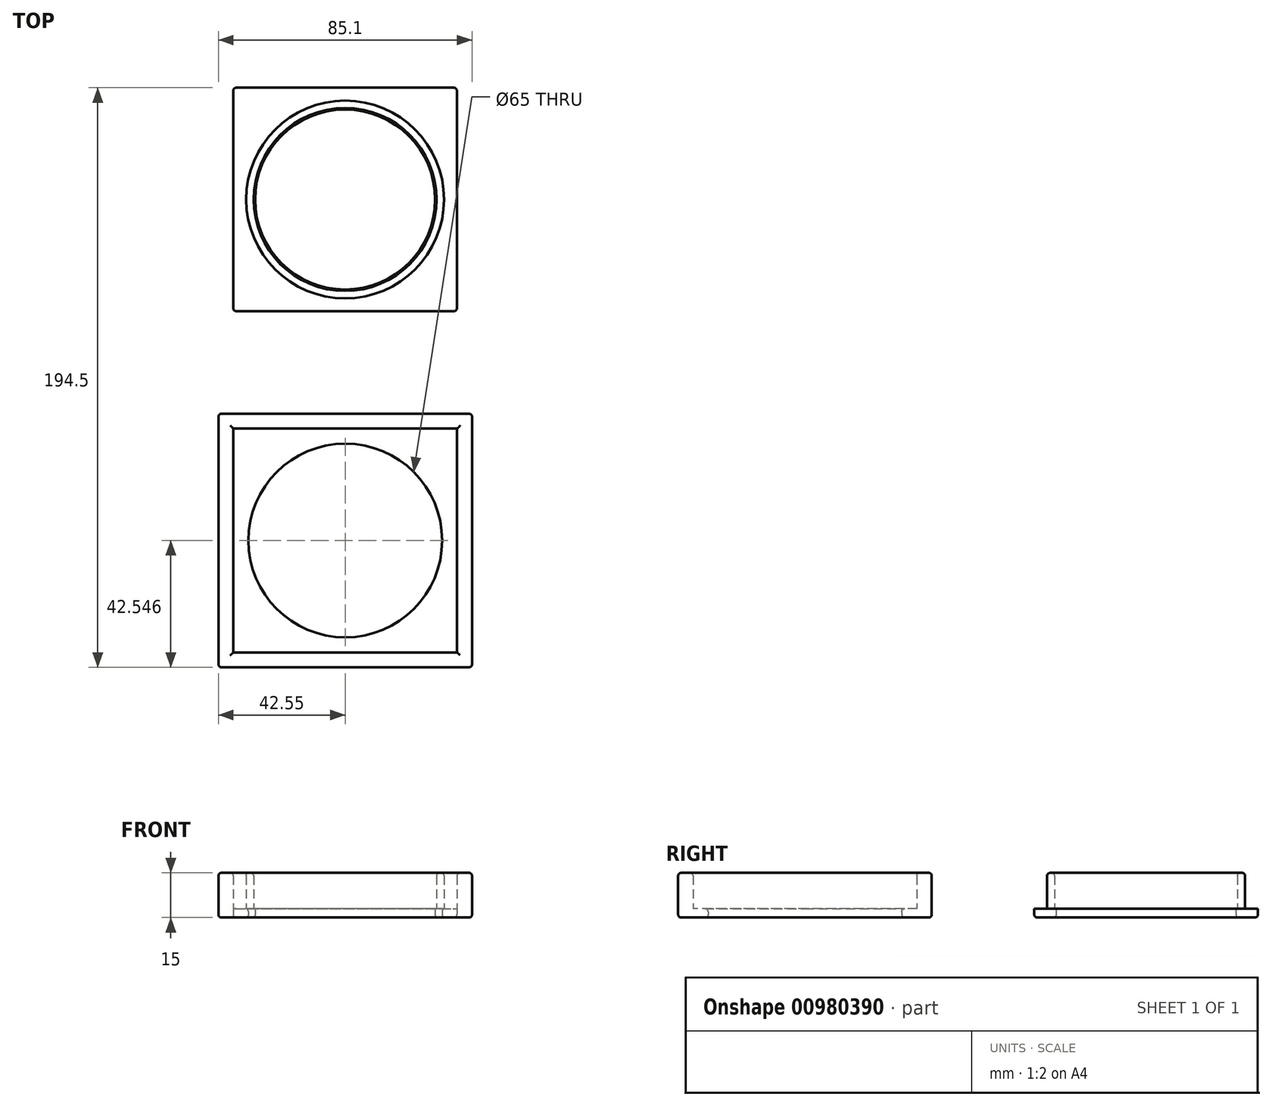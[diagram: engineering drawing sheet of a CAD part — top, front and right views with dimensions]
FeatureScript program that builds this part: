
annotation { "Feature Type Name" : "Feature", "Feature Type Description" : "" }
export const myFeature = defineFeature(function(context is Context, id is Id, definition is map)
    precondition{}
    {
        {
            var Q0;
            Q0=qCreatedBy(makeId("Top.planeOp"),FACE);
            var sketch = newSketch(context, id + "F0", { "sketchPlane" : qUnion([Q0])});
            skLineSegment(sketch, "E0.bottom", {"start": v(0, 0) * mm, "end": v(75, 0) * mm});
            skLineSegment(sketch, "E0.top", {"start": v(0, 75) * mm, "end": v(75, 75) * mm});
            skLineSegment(sketch, "E0.left", {"start": v(0, 0) * mm, "end": v(0, 75) * mm});
            skLineSegment(sketch, "E0.right", {"start": v(75, 0) * mm, "end": v(75, 75) * mm});
            skCircle(sketch, "E1", {"center": v(37.5, 37.5) * mm, "radius": 30.7 * mm});
            skPoint(sketch, "E1.centerSnap0", {"position": v(37.5, 75) * mm});
            skPoint(sketch, "E1.centerSnap1", {"position": v(0, 37.5) * mm});
            skCircle(sketch, "E2", {"center": v(37.5, 37.5) * mm, "radius": 30.2 * mm});
            skCircle(sketch, "E3", {"center": v(37.5, 37.5) * mm, "radius": 33.2 * mm});
            skCircle(sketch, "E4", {"center": v(37.55, -76.95) * mm, "radius": 32.5 * mm});
            skPoint(sketch, "E4.centerSnap1", {"position": v(37.55, -39.4) * mm});
            skLineSegment(sketch, "E5.0", {"start": v(-5, -34.4) * mm, "end": v(80.1, -34.4) * mm});
            skLineSegment(sketch, "E5.1", {"start": v(-5, -34.4) * mm, "end": v(-5, -119.5) * mm});
            skLineSegment(sketch, "E5.2", {"start": v(-5, -119.5) * mm, "end": v(80.1, -119.5) * mm});
            skLineSegment(sketch, "E5.3", {"start": v(80.1, -34.4) * mm, "end": v(80.1, -119.5) * mm});
            skLineSegment(sketch, "E6", {"start": v(0, -114.5) * mm, "end": v(75.1, -114.5) * mm});
            skLineSegment(sketch, "E7", {"start": v(75.1, -39.4) * mm, "end": v(75.1, -114.5) * mm});
            skLineSegment(sketch, "E8", {"start": v(0, -39.4) * mm, "end": v(0, -114.5) * mm});
            skLineSegment(sketch, "E9", {"start": v(0, -39.4) * mm, "end": v(75.1, -39.4) * mm});
            skPoint(sketch, "E10", {"position": v(-5, -76.95) * mm});
            skPoint(sketch, "E11", {"position": v(37.55, -34.4) * mm});
            skSolve(sketch);
        }
        {
            var Q0;
            Q0=makeQuery(id+"F0.imprint","IMPRINT",FACE,{"disambiguationData":[TD([[makeQuery(id+"F0.imprint","IMPRINT",EDGE,{"derivedFrom":sQuery(id+"F0.wireOp",EDGE,"E1")}),-1.0]])]});
            var Q1;
            Q1=makeQuery(id+"F0.imprint","IMPRINT",FACE,{"disambiguationData":[TD([[makeQuery(id+"F0.imprint","IMPRINT",EDGE,{"derivedFrom":sQuery(id+"F0.wireOp",EDGE,"JDFHyrcC-VGeh-v9XD-pVOG-qxKent8c7stP.bottom")}),1.0]])]});
            var Q2;
            Q2=makeQuery(id+"F0.imprint","IMPRINT",FACE,{"disambiguationData":[TD([[makeQuery(id+"F0.imprint","IMPRINT",EDGE,{"derivedFrom":sQuery(id+"F0.wireOp",EDGE,"E5.0")}),-1.0]])]});
            extrude(context, id + "F1", {"entities" : qUnion([Q0, Q1, Q2]), "depth" : 15 * mm, "offsetDistance" : 25 * mm});
        }
        {
            var Q0;
            Q0=makeQuery(id+"F0.imprint","IMPRINT",FACE,{"disambiguationData":[TD([[makeQuery(id+"F0.imprint","IMPRINT",EDGE,{"derivedFrom":sQuery(id+"F0.wireOp",EDGE,"E1")}),1.0]])]});
            var Q1;
            Q1=makeQuery(id+"F0.imprint","IMPRINT",FACE,{"disambiguationData":[TD([[makeQuery(id+"F0.imprint","IMPRINT",EDGE,{"derivedFrom":sQuery(id+"F0.wireOp",EDGE,"E0.bottom")}),1.0]])]});
            var Q2;
            Q2=makeQuery(id+"F0.imprint","IMPRINT",FACE,{"disambiguationData":[TD([[makeQuery(id+"F0.imprint","IMPRINT",EDGE,{"derivedFrom":sQuery(id+"F0.wireOp",EDGE,"JDFHyrcC-VGeh-v9XD-pVOG-qxKent8c7stP.bottom")}),-1.0]])]});
            var Q3;
            Q3=makeQuery(id+"F0.imprint","IMPRINT",FACE,{"disambiguationData":[TD([[makeQuery(id+"F0.imprint","IMPRINT",EDGE,{"derivedFrom":sQuery(id+"F0.wireOp",EDGE,"E4")}),-1.0]])]});
            extrude(context, id + "F2", {"entities" : qUnion([Q0, Q1, Q2, Q3]), "operationType" : NewBodyOperationType.ADD, "depth" : 3 * mm, "offsetDistance" : 25 * mm});
        }
        {
            var Q0;
            Q0=makeQuery(id+"F1.opExtrude","CAP_EDGE",EDGE,{"disambiguationData":[OSD([sQuery(id+"F0.wireOp",EDGE,"E1")])],"isStart":false});
            var Q1;
            Q1=makeQuery(id+"F1.opExtrude","CAP_EDGE",EDGE,{"disambiguationData":[OSD([sQuery(id+"F0.wireOp",EDGE,"E3")])],"isStart":false});
            var Q2;
            Q2=makeQuery(id+"F2.opExtrude","CAP_EDGE",EDGE,{"disambiguationData":[OSD([sQuery(id+"F0.wireOp",EDGE,"E0.bottom")])],"isStart":true});
            var Q3;
            Q3=makeQuery(id+"F2.opExtrude","CAP_EDGE",EDGE,{"disambiguationData":[OSD([sQuery(id+"F0.wireOp",EDGE,"E0.right")])],"isStart":true});
            var Q4;
            Q4=makeQuery(id+"F2.opExtrude","CAP_EDGE",EDGE,{"disambiguationData":[OSD([sQuery(id+"F0.wireOp",EDGE,"E0.top")])],"isStart":true});
            var Q5;
            Q5=makeQuery(id+"F2.opExtrude","CAP_EDGE",EDGE,{"disambiguationData":[OSD([sQuery(id+"F0.wireOp",EDGE,"E0.left")])],"isStart":true});
            var Q6;
            Q6=makeQuery(id+"F2.opExtrude","CAP_EDGE",EDGE,{"disambiguationData":[OSD([sQuery(id+"F0.wireOp",EDGE,"E2")])],"isStart":true});
            var Q7;
            Q7=makeQuery(id+"F1.opExtrude","CAP_EDGE",EDGE,{"disambiguationData":[OSD([sQuery(id+"F0.wireOp",EDGE,"E5.3")])],"isStart":false});
            var Q8;
            Q8=makeQuery(id+"F1.opExtrude","CAP_EDGE",EDGE,{"disambiguationData":[OSD([sQuery(id+"F0.wireOp",EDGE,"E5.0")])],"isStart":false});
            var Q9;
            Q9=makeQuery(id+"F1.opExtrude","CAP_EDGE",EDGE,{"disambiguationData":[OSD([sQuery(id+"F0.wireOp",EDGE,"E5.1")])],"isStart":false});
            var Q10;
            Q10=makeQuery(id+"F1.opExtrude","CAP_EDGE",EDGE,{"disambiguationData":[OSD([sQuery(id+"F0.wireOp",EDGE,"E5.2")])],"isStart":false});
            var Q11;
            Q11=makeQuery(id+"F1.opExtrude","SWEPT_EDGE",EDGE,{"disambiguationData":[OSD([sQuery(id+"F0.wireOp",EDGE,"E5.1"),sQuery(id+"F0.wireOp",EDGE,"E5.2")])]});
            var Q12;
            Q12=makeQuery(id+"F1.opExtrude","SWEPT_EDGE",EDGE,{"disambiguationData":[OSD([sQuery(id+"F0.wireOp",EDGE,"E5.2"),sQuery(id+"F0.wireOp",EDGE,"E5.3")])]});
            var Q13;
            Q13=makeQuery(id+"F1.opExtrude","SWEPT_EDGE",EDGE,{"disambiguationData":[OSD([sQuery(id+"F0.wireOp",EDGE,"E5.0"),sQuery(id+"F0.wireOp",EDGE,"E5.3")])]});
            var Q14;
            Q14=makeQuery(id+"F1.opExtrude","SWEPT_EDGE",EDGE,{"disambiguationData":[OSD([sQuery(id+"F0.wireOp",EDGE,"E5.0"),sQuery(id+"F0.wireOp",EDGE,"E5.1")])]});
            var Q15;
            Q15=makeQuery(id+"F1.opExtrude","CAP_EDGE",EDGE,{"disambiguationData":[OSD([sQuery(id+"F0.wireOp",EDGE,"E5.0")])],"isStart":true});
            var Q16;
            Q16=makeQuery(id+"F1.opExtrude","CAP_EDGE",EDGE,{"disambiguationData":[OSD([sQuery(id+"F0.wireOp",EDGE,"E5.3")])],"isStart":true});
            var Q17;
            Q17=makeQuery(id+"F2.opExtrude","CAP_EDGE",EDGE,{"disambiguationData":[OSD([sQuery(id+"F0.wireOp",EDGE,"E4")])],"isStart":true});
            var Q18;
            Q18=makeQuery(id+"F1.opExtrude","CAP_EDGE",EDGE,{"disambiguationData":[OSD([sQuery(id+"F0.wireOp",EDGE,"E5.1")])],"isStart":true});
            var Q19;
            Q19=makeQuery(id+"F1.opExtrude","CAP_EDGE",EDGE,{"disambiguationData":[OSD([sQuery(id+"F0.wireOp",EDGE,"E5.2")])],"isStart":true});
            var Q20;
            Q20=makeQuery(id+"F2.opExtrude","CAP_EDGE",EDGE,{"disambiguationData":[OSD([sQuery(id+"F0.wireOp",EDGE,"E4")])],"isStart":false});
            var Q21;
            Q21=makeQuery(id+"F2.opExtrude","SWEPT_EDGE",EDGE,{"disambiguationData":[OSD([sQuery(id+"F0.wireOp",EDGE,"E0.top"),sQuery(id+"F0.wireOp",EDGE,"E0.right")])]});
            var Q22;
            Q22=makeQuery(id+"F2.opExtrude","SWEPT_EDGE",EDGE,{"disambiguationData":[OSD([sQuery(id+"F0.wireOp",EDGE,"E0.top"),sQuery(id+"F0.wireOp",EDGE,"E0.left")])]});
            var Q23;
            Q23=makeQuery(id+"F2.opExtrude","SWEPT_EDGE",EDGE,{"disambiguationData":[OSD([sQuery(id+"F0.wireOp",EDGE,"E0.bottom"),sQuery(id+"F0.wireOp",EDGE,"E0.left")])]});
            var Q24;
            Q24=makeQuery(id+"F2.opExtrude","SWEPT_EDGE",EDGE,{"disambiguationData":[OSD([sQuery(id+"F0.wireOp",EDGE,"E0.bottom"),sQuery(id+"F0.wireOp",EDGE,"E0.right")])]});
            var Q25;
            Q25=makeQuery(id+"F1.opExtrude","CAP_EDGE",EDGE,{"disambiguationData":[OSD([sQuery(id+"F0.wireOp",EDGE,"E8")])],"isStart":false});
            var Q26;
            Q26=makeQuery(id+"F1.opExtrude","CAP_EDGE",EDGE,{"disambiguationData":[OSD([sQuery(id+"F0.wireOp",EDGE,"E9")])],"isStart":false});
            var Q27;
            Q27=makeQuery(id+"F1.opExtrude","CAP_EDGE",EDGE,{"disambiguationData":[OSD([sQuery(id+"F0.wireOp",EDGE,"E7")])],"isStart":false});
            var Q28;
            Q28=makeQuery(id+"F1.opExtrude","CAP_EDGE",EDGE,{"disambiguationData":[OSD([sQuery(id+"F0.wireOp",EDGE,"E6")])],"isStart":false});
            var Q29;
            Q29=makeQuery(id+"F2.opExtrude","CAP_EDGE",EDGE,{"disambiguationData":[OSD([sQuery(id+"F0.wireOp",EDGE,"E3")])],"isStart":false});
            fillet(context, id + "F3", {"entities" : qUnion([Q0, Q1, Q2, Q3, Q4, Q5, Q6, Q7, Q8, Q9, Q10, Q11, Q12, Q13, Q14, Q15, Q16, Q17, Q18, Q19, Q20, Q21, Q22, Q23, Q24, Q25, Q26, Q27, Q28, Q29]), "radius" : 1 * mm, "tangentPropagation" : true, "allowEdgeOverflow" : false});
        }
    });
